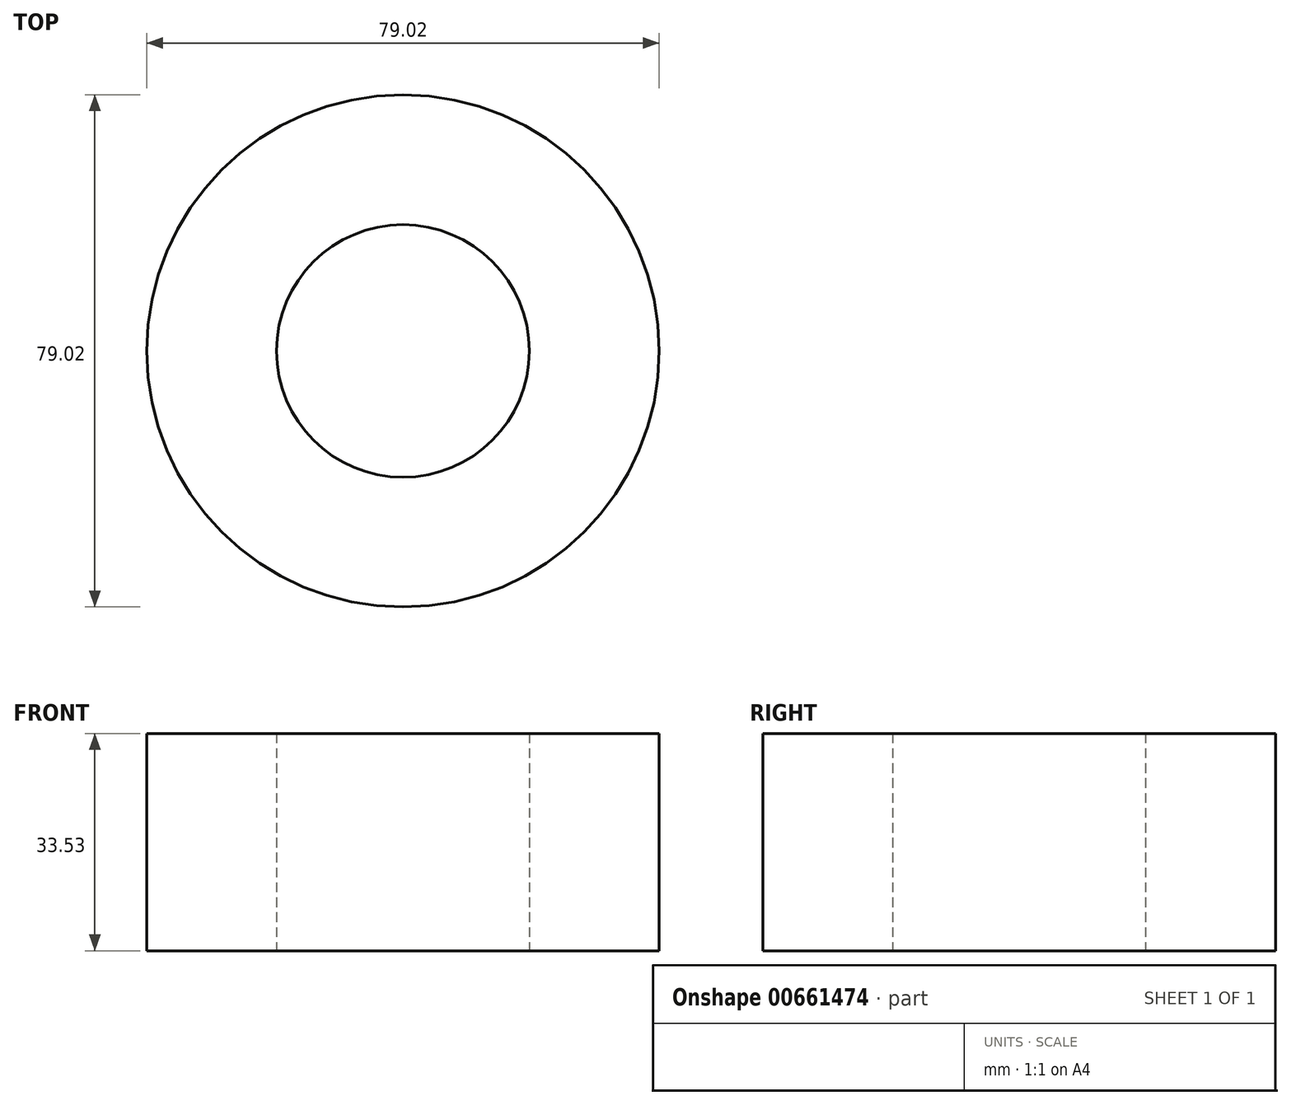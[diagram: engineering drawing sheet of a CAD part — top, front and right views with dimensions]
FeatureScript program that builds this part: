
annotation { "Feature Type Name" : "Feature", "Feature Type Description" : "" }
export const myFeature = defineFeature(function(context is Context, id is Id, definition is map)
    precondition{}
    {
        {
            var Q0;
            Q0=qCreatedBy(makeId("Top.planeOp"),FACE);
            var sketch = newSketch(context, id + "F0", { "sketchPlane" : qUnion([Q0])});
            skCircle(sketch, "E0", {"center": v(0, 0) * mm, "radius": 19.49 * mm});
            skCircle(sketch, "E1", {"center": v(0, 0) * mm, "radius": 39.5 * mm});
            skSolve(sketch);
        }
        {
            var Q0;
            Q0 = qSketchRegion(id + "F0", true);
            extrude(context, id + "F1", {"entities" : qUnion([Q0]), "depth" : 33.53 * mm, "offsetDistance" : 25.4 * mm});
        }
    });
